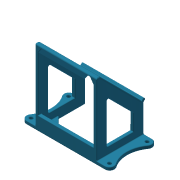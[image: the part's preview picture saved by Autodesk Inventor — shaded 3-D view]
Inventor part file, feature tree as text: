
AUTODESK INVENTOR PART (.ipt)
format: ipt  version: 2014 (Build 180170000, 170)  size: 473,600 bytes
history: native  units: mm
features: fillet x12, extrude x6, sketch x4, chamfer x2
ambient origin geometry x8: Origin, YZ Plane, XZ Plane, XY Plane, X Axis, Y Axis, Z Axis, Center Point
bodies: Solid1 (feature_tree)
feature tree (24):
  extrude  "Extrusion1"  Depth=90.0mm
  extrude  "Extrusion2"  Depth=90.0mm TaperAngle=0.0deg
  extrude  "Extrusion3"  Depth=12.0mm
  extrude  "Extrusion4"  Depth=5.0mm TaperAngle=0.0deg
  extrude  "Extrusion7"  Depth=1.0mm
  chamfer  "Chamfer2"  Distance=4.0mm
  extrude  "Extrusion9"  Depth=80.0mm TaperAngle=0.0deg
  chamfer  "Chamfer4"  Distance=15.0mm
  fillet  "Fillet1"  Radius=15.0mm
  fillet  "Fillet3"  Radius=140.0mm
  fillet  "Fillet4"  Radius=5.0mm
  fillet  "Fillet5"  Radius=2.0mm
  fillet  "Fillet6"  Radius=2.0mm
  fillet  "Fillet7"  Radius=1.0mm
  fillet  "Fillet12"  Radius=1.0mm
  fillet  "Fillet15"  Radius=1.0mm
  fillet  "Fillet16"  Radius=1.0mm
  fillet  "Fillet17"  Radius=1.0mm
  fillet  "Fillet18"  Radius=1.0mm
  fillet  "Fillet19"  Radius=1.0mm
  sketch  "Sketch1"  dims[d0=45.0deg d1=90.0mm]
  sketch  "Sketch3"  dims[d2=45.0mm d3=90.0mm d4=0.0mm]
  sketch  "Sketch7"  dims[d5=4.5mm d6=12.0mm]
  sketch  "Sketch9"  dims[d7=7.0mm d8=5.0mm d9=0.0mm d10=4.0mm d11=4.0mm d12=0.0mm d14=80.0mm d15=0.0mm d26=15.0mm d27=15.0mm d28=15.0mm d29=140.0mm d30=0.0mm d34=5.0mm d35=2.0mm d36=45.0deg d46=2.0mm d48=2.0mm d49=1.0mm d50=1.0mm d51=1.0mm d52=1.0mm d57=1.0mm d60=1.0mm d61=1.0mm d62=108.63961mm d63=5.0mm d64=15.0mm d66=5.0mm d67=40.0mm d68=15.0mm d69=5.0mm d70=20.0mm d71=10.0mm d72=0.0mm d73=10.0mm d74=2.0mm d75=45.0deg d76=1.0mm d77=1.0mm d78=1.0mm]
